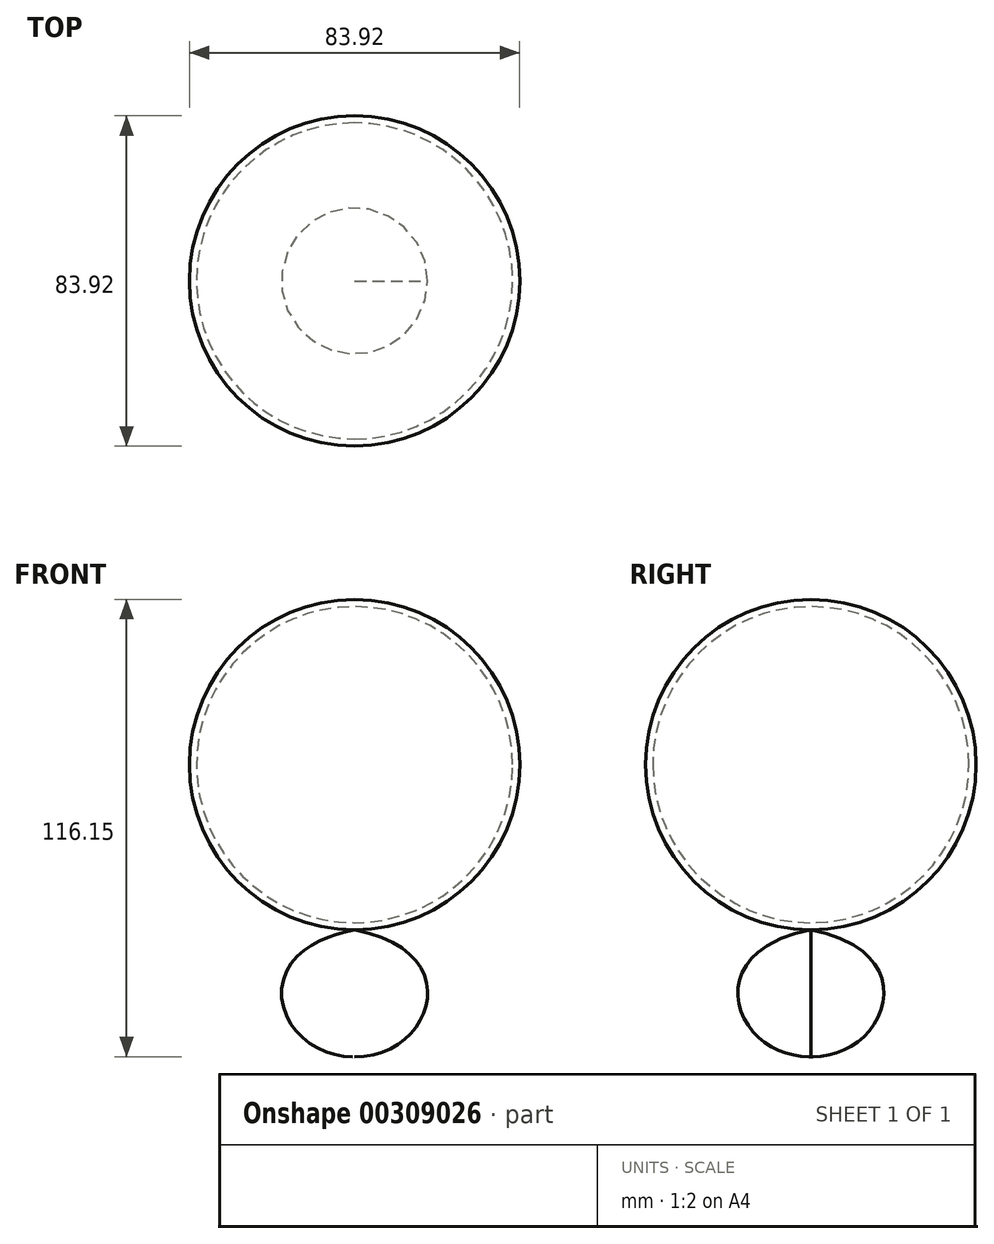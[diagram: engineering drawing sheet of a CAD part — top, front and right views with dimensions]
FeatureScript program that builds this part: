
annotation { "Feature Type Name" : "Feature", "Feature Type Description" : "" }
export const myFeature = defineFeature(function(context is Context, id is Id, definition is map)
    precondition{}
    {
        {
            var Q0;
            Q0=qCreatedBy(makeId("Top.planeOp"),FACE);
            var sketch = newSketch(context, id + "F0", { "sketchPlane" : qUnion([Q0])});
            skArc(sketch, "E0", {"start": v(0, -40.15) * mm, "mid": v(40.15, 0) * mm, "end": v(0, 40.15) * mm});
            skArc(sketch, "E1", {"start": v(0, -41.96) * mm, "mid": v(41.96, 0) * mm, "end": v(0, 41.96) * mm});
            skLineSegment(sketch, "E2", {"start": v(0, 41.96) * mm, "end": v(0, 40.15) * mm});
            skLineSegment(sketch, "E3.trimOffspring", {"start": v(0, -40.15) * mm, "end": v(0, -41.96) * mm});
            skLineSegment(sketch, "E4", {"start": v(0, 41.96) * mm, "end": v(0, -41.96) * mm, "construction": true});
            skLineSegment(sketch, "E5", {"start": v(0, 0) * mm, "end": v(41.96, 0) * mm, "construction": true});
            skSolve(sketch);
        }
        {
            var Q0;
            Q0=qCreatedBy(makeId("Front.planeOp"),FACE);
            var sketch = newSketch(context, id + "F1", { "sketchPlane" : qUnion([Q0])});
            skLineSegment(sketch, "E6", {"start": v(0, -41.95) * mm, "end": v(0, -41.95) * mm});
            skFitSpline(sketch, "E7", {"points": [v(0, -41.95) * mm, v(0, -74.19) * mm], "startDerivative": vector(88.9, -16.74) * mm, "endDerivative": vector(-57.87, 1.38) * mm});
            skLineSegment(sketch, "E8", {"start": v(0, -41.95) * mm, "end": v(0, -74.19) * mm});
            skLineSegment(sketch, "E9", {"start": v(0, 0) * mm, "end": v(0, -41.94) * mm, "construction": true});
            skSolve(sketch);
        }
        {
            var Q0;
            Q0=makeQuery(id+"F0.imprint","IMPRINT",FACE,{"disambiguationData":[TD([[makeQuery(id+"F0.imprint","IMPRINT",EDGE,{"derivedFrom":sQuery(id+"F0.wireOp",EDGE,"E0")}),-1.0]])]});
            var Q1;
            Q1=sQuery(id+"F0.wireOp",EDGE,"E4");
            revolve(context, id + "F2", {"entities" : qUnion([Q0]), "axis" : qUnion([Q1]), "revolveType" : RevolveType.FULL});
        }
        {
            var Q0;
            Q0=makeQuery(id+"F1.imprint","IMPRINT",FACE,{"disambiguationData":[TD([[makeQuery(id+"F1.imprint","IMPRINT",EDGE,{"derivedFrom":sQuery(id+"F1.wireOp",EDGE,"E7")}),-1.0]])]});
            var Q1;
            Q1=sQuery(id+"F1.wireOp",EDGE,"E8");
            revolve(context, id + "F3", {"entities" : qUnion([Q0]), "axis" : qUnion([Q1]), "revolveType" : RevolveType.FULL});
        }
    });
